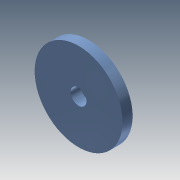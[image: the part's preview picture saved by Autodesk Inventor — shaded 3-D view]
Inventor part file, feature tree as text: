
AUTODESK INVENTOR PART (.ipt)
format: ipt  version: 2013 (Build 170138000, 138)  size: 111,616 bytes
history: native  units: mm
features: extrude x6, sketch x6
ambient origin geometry x8: Origin, YZ Plane, XZ Plane, XY Plane, X Axis, Y Axis, Z Axis, Center Point
bodies: Solid1 (feature_tree)
feature tree (12):
  extrude  "Extrusion1"  Depth=3.8mm TaperAngle=0.0deg
  extrude  "Extrusion2"  Depth=1.0mm TaperAngle=0.0deg
  extrude  "Extrusion3"  Depth=3.8mm TaperAngle=0.0deg
  extrude  "Extrusion4"  Depth=3.6mm TaperAngle=0.0deg
  extrude  "Extrusion5"  Depth=3.6mm TaperAngle=0.0deg
  extrude  "Extrusion6"  Depth=3.8mm TaperAngle=0.0deg
  sketch  "Sketch1"  dims[d0=33.15mm d1=3.8mm d2=0.0mm]
  sketch  "Sketch2"  dims[d3=28.0mm d4=1.0mm d5=0.0mm]
  sketch  "Sketch3"  dims[d6=10.0mm d7=3.8mm d8=0.0mm]
  sketch  "Sketch4"  dims[d9=3.6mm d10=3.6mm d11=0.0mm]
  sketch  "Sketch5"  dims[d12=6.0mm d13=3.6mm d14=0.0mm]
  sketch  "Sketch6"  dims[d15=6.0mm d16=3.8mm d17=0.0mm]
